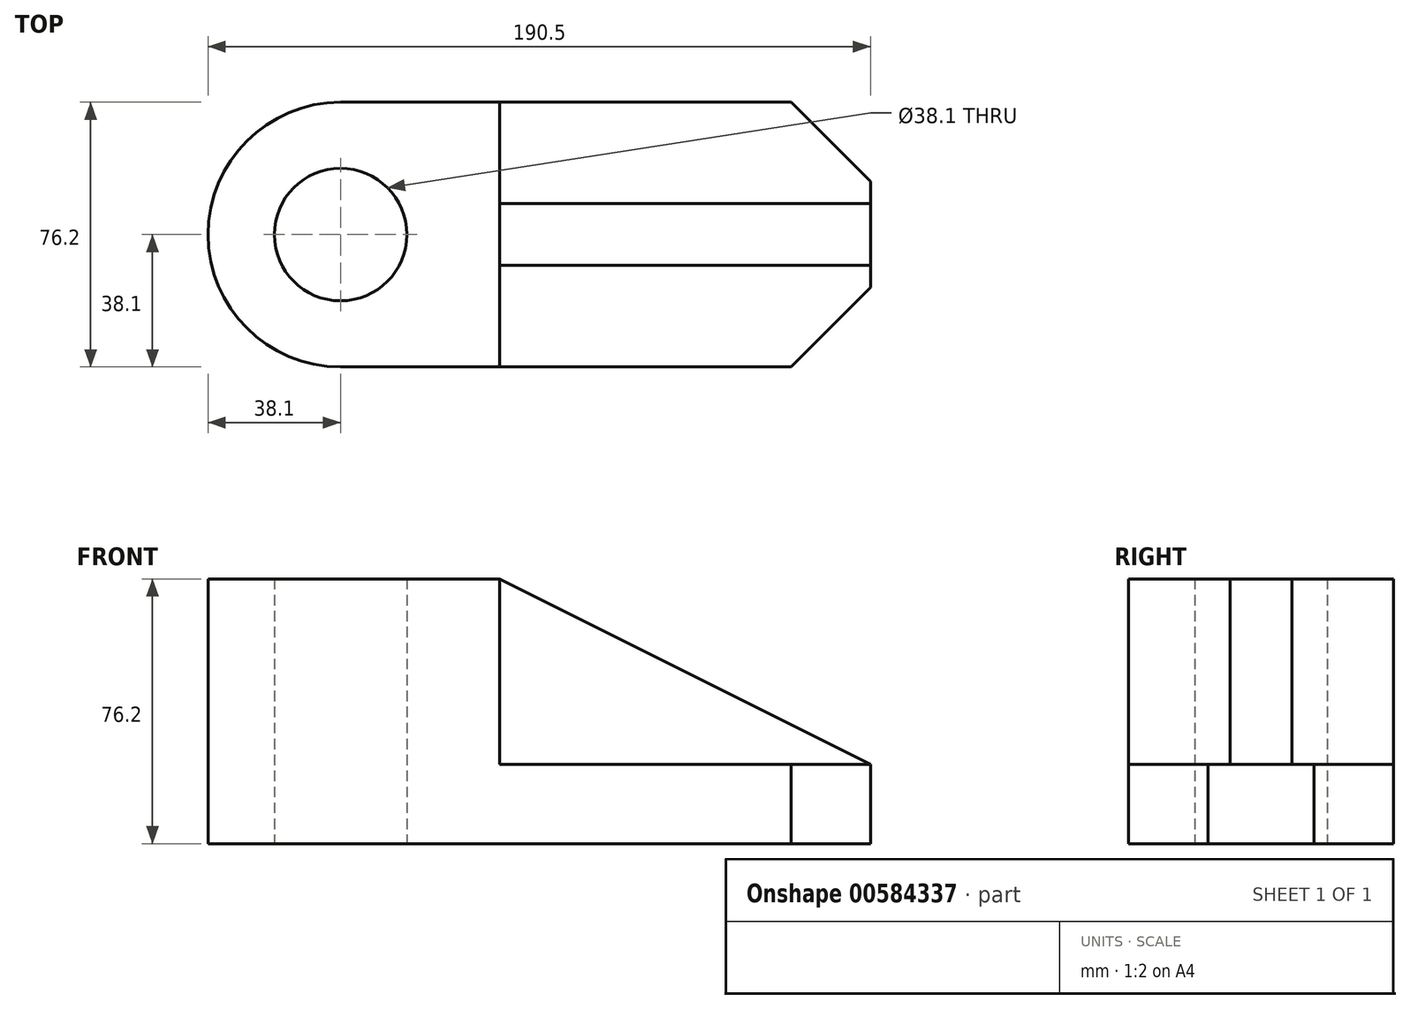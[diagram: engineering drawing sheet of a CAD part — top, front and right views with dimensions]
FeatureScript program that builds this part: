
annotation { "Feature Type Name" : "Feature", "Feature Type Description" : "" }
export const myFeature = defineFeature(function(context is Context, id is Id, definition is map)
    precondition{}
    {
        {
            var Q0;
            Q0=qCreatedBy(makeId("Top.planeOp"),FACE);
            var sketch = newSketch(context, id + "F0", { "sketchPlane" : qUnion([Q0])});
            skArc(sketch, "E0", {"start": v(-152.4, 38.1) * mm, "mid": v(-190.5, 0) * mm, "end": v(-152.4, -38.1) * mm});
            skCircle(sketch, "E1", {"center": v(-152.4, 0) * mm, "radius": 19.05 * mm});
            skLineSegment(sketch, "E2", {"start": v(-152.4, 38.1) * mm, "end": v(-22.86, 38.1) * mm});
            skLineSegment(sketch, "E3", {"start": v(-152.4, -38.1) * mm, "end": v(-22.86, -38.1) * mm});
            skLineSegment(sketch, "E4", {"start": v(0, -15.24) * mm, "end": v(0, 15.24) * mm});
            skLineSegment(sketch, "E5", {"start": v(-22.86, 38.1) * mm, "end": v(0, 15.24) * mm});
            skLineSegment(sketch, "E6", {"start": v(-22.86, -38.1) * mm, "end": v(0, -15.24) * mm});
            skLineSegment(sketch, "E7", {"start": v(-106.68, 38.1) * mm, "end": v(-106.68, -38.1) * mm});
            skLineSegment(sketch, "E8", {"start": v(-106.68, 8.89) * mm, "end": v(0, 8.9) * mm});
            skLineSegment(sketch, "E9", {"start": v(-106.68, -8.9) * mm, "end": v(0, -8.9) * mm});
            skSolve(sketch);
        }
        {
            var Q0;
            {var subQ1=sQuery(id+"F0.wireOp",EDGE,"E0");Q0=makeQuery(id+"F0.imprint","IMPRINT",FACE,{"disambiguationData":[TD([[makeQuery(id+"F0.imprint","IMPRINT",EDGE,{"derivedFrom":subQ1}),1.0]])]});}
            extrude(context, id + "F1", {"entities" : qUnion([Q0]), "depth" : 76.2 * mm, "offsetDistance" : 25.4 * mm});
        }
        {
            var Q0;
            {var subQ4=sQuery(id+"F0.wireOp",EDGE,"E6");Q0=makeQuery(id+"F0.imprint","IMPRINT",FACE,{"disambiguationData":[TD([[makeQuery(id+"F0.imprint","IMPRINT",EDGE,{"derivedFrom":subQ4}),1.0]])]});}
            var Q1;
            {var subQ4=sQuery(id+"F0.wireOp",EDGE,"E5");Q1=makeQuery(id+"F0.imprint","IMPRINT",FACE,{"disambiguationData":[TD([[makeQuery(id+"F0.imprint","IMPRINT",EDGE,{"derivedFrom":subQ4}),-1.0]])]});}
            extrude(context, id + "F2", {"entities" : qUnion([Q0, Q1]), "operationType" : NewBodyOperationType.ADD, "depth" : 22.86 * mm, "offsetDistance" : 25.4 * mm});
        }
        {
            var Q0;
            {var subQ0=sQuery(id+"F0.wireOp",EDGE,"E8");Q0=makeQuery(id+"F0.imprint","IMPRINT",FACE,{"disambiguationData":[TD([[makeQuery(id+"F0.imprint","IMPRINT",EDGE,{"derivedFrom":subQ0}),-1.0]])]});}
            extrude(context, id + "F3", {"entities" : qUnion([Q0]), "operationType" : NewBodyOperationType.ADD, "depth" : 76.2 * mm, "offsetDistance" : 25.4 * mm});
        }
        {
            var Q0;
            Q0=makeQuery(id+"F3.opExtrude","SWEPT_FACE",FACE,{"disambiguationData":[OSD([sQuery(id+"F0.wireOp",EDGE,"E9")])]});
            var sketch = newSketch(context, id + "F4", { "sketchPlane" : qUnion([Q0])});
            skLineSegment(sketch, "E10", {"start": v(-106.68, 76.2) * mm, "end": v(0, 22.86) * mm});
            skSolve(sketch);
        }
        {
            var Q0;
            Q0=makeQuery(id+"F4.imprint","IMPRINT",FACE,{"disambiguationData":[TD([[makeQuery(id+"F4.imprint","IMPRINT",EDGE,{"derivedFrom":sQuery(id+"F4.wireOp",EDGE,"E10")}),1.0]])]});
            extrude(context, id + "F5", {"entities" : qUnion([Q0]), "operationType" : NewBodyOperationType.REMOVE, "oppositeDirection" : true, "depth" : 254 * mm, "offsetDistance" : 25.4 * mm});
        }
    });
